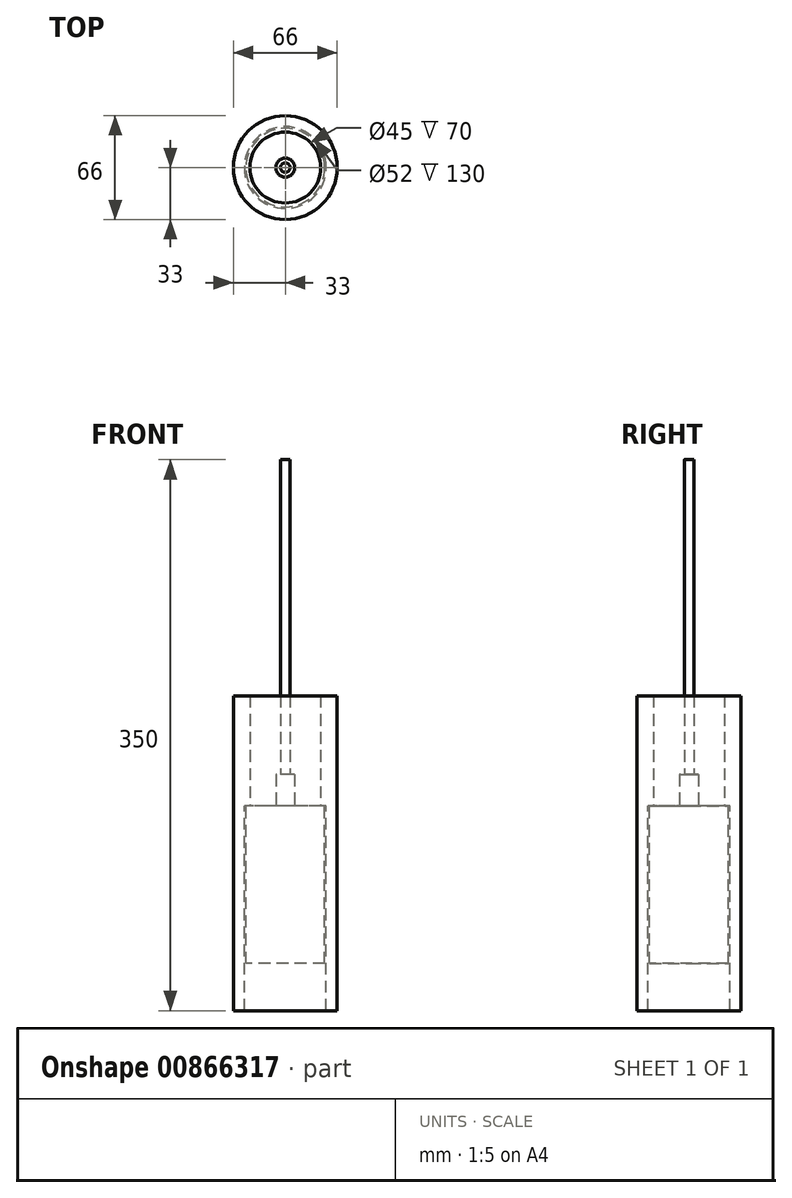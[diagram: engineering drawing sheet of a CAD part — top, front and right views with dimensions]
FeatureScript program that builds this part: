
annotation { "Feature Type Name" : "Feature", "Feature Type Description" : "" }
export const myFeature = defineFeature(function(context is Context, id is Id, definition is map)
    precondition{}
    {
        {
            var Q0;
            Q0=qCreatedBy(makeId("Top.planeOp"),FACE);
            var sketch = newSketch(context, id + "F0", { "sketchPlane" : qUnion([Q0])});
            skCircle(sketch, "E0", {"center": v(0, 0) * mm, "radius": 26 * mm, "construction": true});
            skCircle(sketch, "E1", {"center": v(0, 0) * mm, "radius": 33 * mm});
            skSolve(sketch);
        }
        {
            var Q0;
            Q0=qSketchRegion(id+"F0",true);
            extrude(context, id + "F1", {"entities" : qUnion([Q0]), "oppositeDirection" : true, "depth" : 200 * mm, "offsetDistance" : 25 * mm});
        }
        {
            var Q0;
            Q0=qCreatedBy(makeId("Top.planeOp"),FACE);
            cPlane(context, id + "F2", {"entities" : qUnion([Q0]), "cplaneType" : CPlaneType.OFFSET, "offset" : 70 * mm, "oppositeDirection" : true, "width" : 150 * mm, "height" : 150 * mm});
        }
        {
            var Q0;
            Q0=qCreatedBy(id+"F2.planeOp",FACE);
            var sketch = newSketch(context, id + "F3", { "sketchPlane" : qUnion([Q0])});
            skCircle(sketch, "E2.0", {"center": v(0, 0) * mm, "radius": 26 * mm, "construction": true});
            skCircle(sketch, "E3", {"center": v(0, 0) * mm, "radius": 22.5 * mm});
            skSolve(sketch);
        }
        {
            var Q0;
            Q0 = qSketchRegion(id + "F3", true);
            extrude(context, id + "F4", {"entities" : qUnion([Q0]), "operationType" : NewBodyOperationType.REMOVE, "endBound" : BoundingType.THROUGH_ALL, "depth" : 25 * mm, "offsetDistance" : 25 * mm});
        }
        {
            var Q0;
            Q0=qCreatedBy(id+"F2.planeOp",FACE);
            var sketch = newSketch(context, id + "F5", { "sketchPlane" : qUnion([Q0])});
            skCircle(sketch, "E4.0", {"center": v(0, 0) * mm, "radius": 26 * mm});
            skSolve(sketch);
        }
        {
            var Q0;
            Q0 = qSketchRegion(id + "F5", true);
            extrude(context, id + "F6", {"entities" : qUnion([Q0]), "operationType" : NewBodyOperationType.REMOVE, "endBound" : BoundingType.THROUGH_ALL, "oppositeDirection" : true, "depth" : 25 * mm, "offsetDistance" : 25 * mm});
        }
        {
            var Q0;
            Q0=qCreatedBy(id+"F2.planeOp",FACE);
            var sketch = newSketch(context, id + "F7", { "sketchPlane" : qUnion([Q0])});
            skCircle(sketch, "E5", {"center": v(0, 0) * mm, "radius": 25 * mm});
            skSolve(sketch);
        }
        {
            var Q0;
            Q0=qSketchRegion(id+"F7",true);
            extrude(context, id + "F8", {"entities" : qUnion([Q0]), "oppositeDirection" : true, "depth" : 100 * mm, "offsetDistance" : 25 * mm});
        }
        {
            var Q0;
            Q0=makeQuery(id+"F8.opExtrude","CAP_FACE",FACE,{"disambiguationData":[OSD([sQuery(id+"F7.wireOp",EDGE,"E5")])],"isStart":true});
            var sketch = newSketch(context, id + "F9", { "sketchPlane" : qUnion([Q0])});
            skCircle(sketch, "E6", {"center": v(0, 0) * mm, "radius": 6 * mm});
            skSolve(sketch);
        }
        {
            var Q0;
            Q0=qSketchRegion(id+"F9",true);
            extrude(context, id + "F10", {"entities" : qUnion([Q0]), "operationType" : NewBodyOperationType.ADD, "depth" : 20 * mm, "offsetDistance" : 25 * mm});
        }
        {
            var Q0;
            Q0=makeQuery(id+"F10.opExtrude","CAP_FACE",FACE,{"disambiguationData":[OSD([sQuery(id+"F9.wireOp",EDGE,"E6")])],"isStart":false});
            var sketch = newSketch(context, id + "F11", { "sketchPlane" : qUnion([Q0])});
            skCircle(sketch, "E7", {"center": v(0, 0) * mm, "radius": 3 * mm});
            skSolve(sketch);
        }
        {
            var Q0;
            Q0=qSketchRegion(id+"F11",true);
            extrude(context, id + "F12", {"entities" : qUnion([Q0]), "operationType" : NewBodyOperationType.ADD, "depth" : 200 * mm, "offsetDistance" : 25 * mm});
        }
    });
